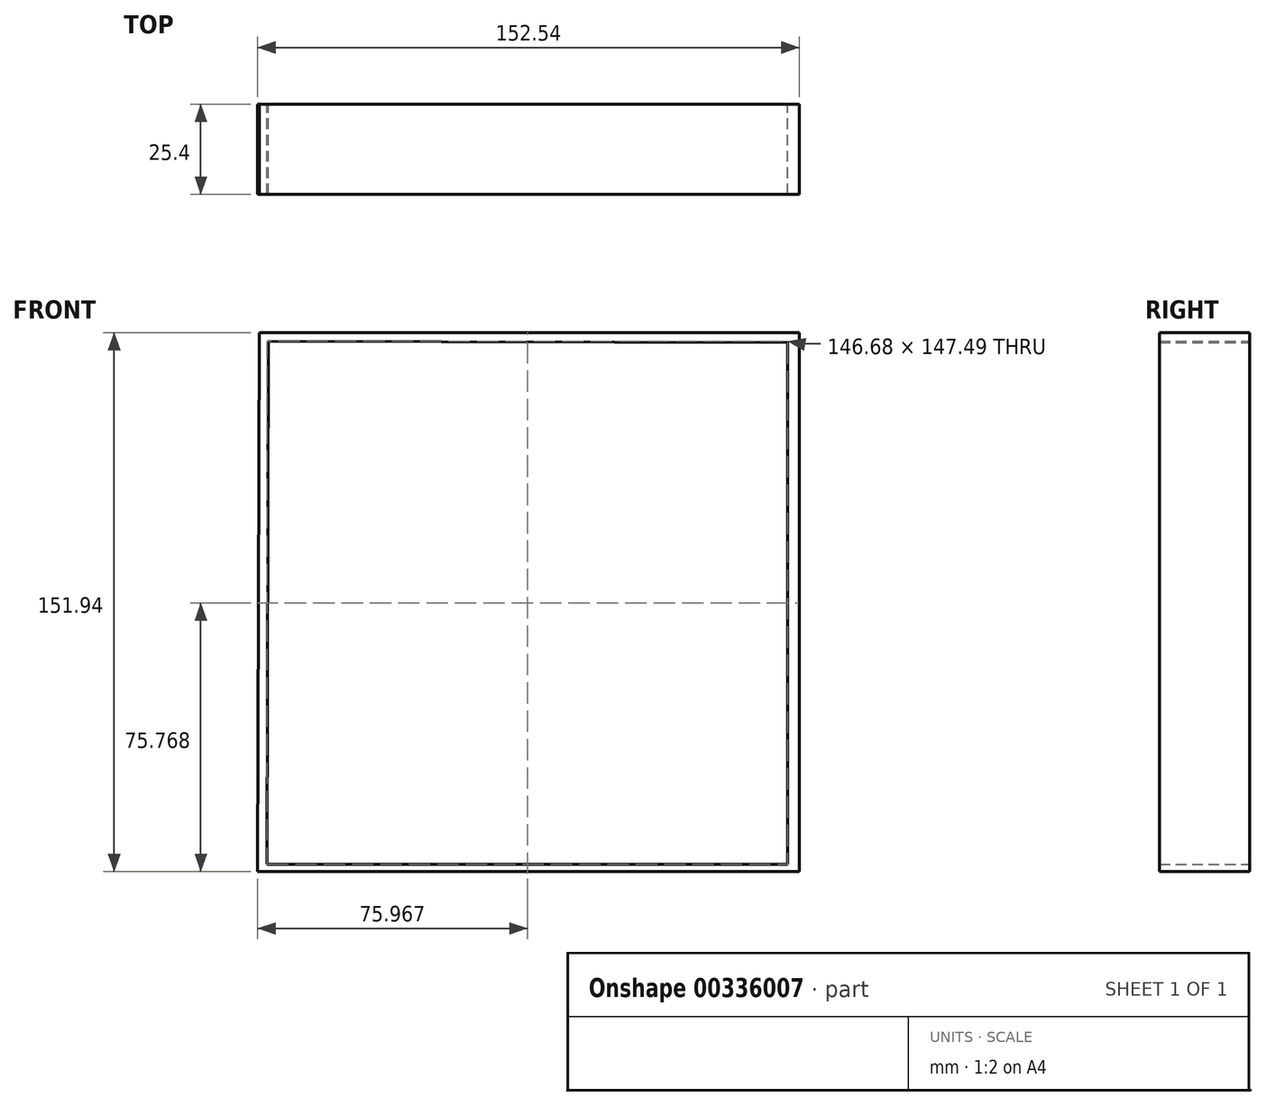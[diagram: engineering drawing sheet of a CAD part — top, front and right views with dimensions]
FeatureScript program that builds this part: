
annotation { "Feature Type Name" : "Feature", "Feature Type Description" : "" }
export const myFeature = defineFeature(function(context is Context, id is Id, definition is map)
    precondition{}
    {
        {
            var Q0;
            Q0=qCreatedBy(makeId("Front.planeOp"),FACE);
            var sketch = newSketch(context, id + "F0", { "sketchPlane" : qUnion([Q0])});
            skLineSegment(sketch, "E0", {"start": v(-75.77, 75.97) * mm, "end": v(76.37, 75.97) * mm});
            skLineSegment(sketch, "E1", {"start": v(76.37, 75.97) * mm, "end": v(76.37, -75.97) * mm});
            skLineSegment(sketch, "E2", {"start": v(76.37, -75.97) * mm, "end": v(-76.17, -75.97) * mm});
            skLineSegment(sketch, "E3", {"start": v(-75.77, 75.97) * mm, "end": v(-76.17, -75.97) * mm});
            skLineSegment(sketch, "E4", {"start": v(-73.14, 73.54) * mm, "end": v(73.14, 73.16) * mm});
            skLineSegment(sketch, "E5", {"start": v(73.14, 73.16) * mm, "end": v(73.14, -71.32) * mm});
            skLineSegment(sketch, "E6", {"start": v(73.14, -71.32) * mm, "end": v(73.14, -49.1) * mm});
            skLineSegment(sketch, "E7", {"start": v(73.14, -71.32) * mm, "end": v(73.14, -73.95) * mm});
            skLineSegment(sketch, "E8", {"start": v(73.14, -73.95) * mm, "end": v(-73.54, -73.95) * mm});
            skLineSegment(sketch, "E9", {"start": v(-73.54, -73.95) * mm, "end": v(-73.14, 73.54) * mm});
            skSolve(sketch);
        }
        {
            var Q0;
            Q0=makeQuery(id+"F0.imprint","IMPRINT",FACE,{"disambiguationData":[TD([[makeQuery(id+"F0.imprint","IMPRINT",EDGE,{"derivedFrom":sQuery(id+"F0.wireOp",EDGE,"E0")}),-1.0]])]});
            extrude(context, id + "F1", {"entities" : qUnion([Q0]), "depth" : 25.4 * mm});
        }
    });
